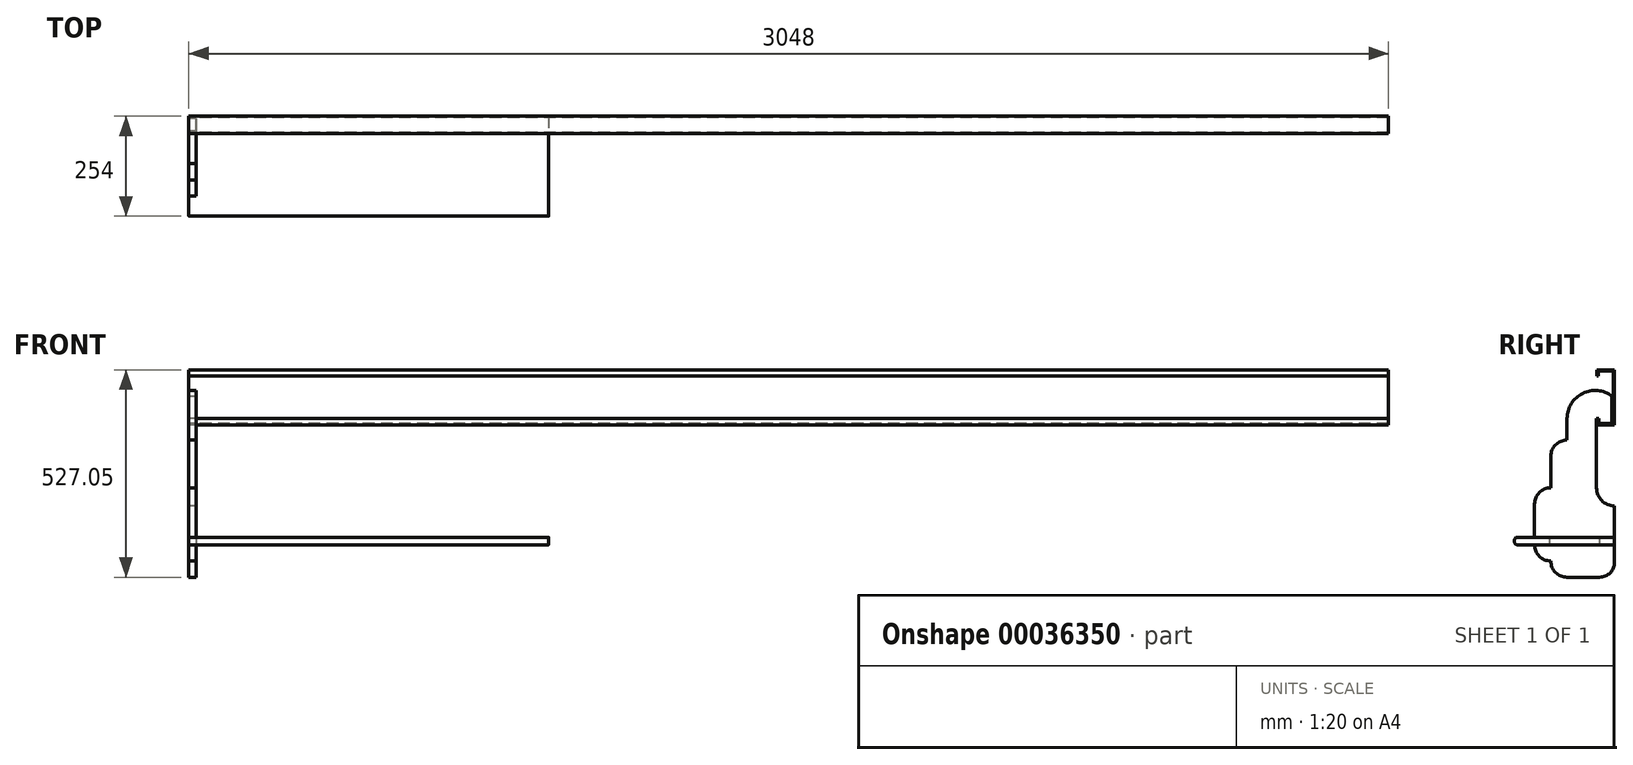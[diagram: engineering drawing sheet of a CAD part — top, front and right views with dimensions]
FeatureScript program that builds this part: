
annotation { "Feature Type Name" : "Feature", "Feature Type Description" : "" }
export const myFeature = defineFeature(function(context is Context, id is Id, definition is map)
    precondition{}
    {
        {
            var Q0;
            Q0=qCreatedBy(makeId("Right.planeOp"),FACE);
            var sketch = newSketch(context, id + "F0", { "sketchPlane" : qUnion([Q0])});
            skLineSegment(sketch, "E0", {"start": v(-44.45, 123.83) * mm, "end": v(-44.45, 139.7) * mm});
            skLineSegment(sketch, "E1", {"start": v(-44.45, 139.7) * mm, "end": v(0, 139.7) * mm});
            skLineSegment(sketch, "E2", {"start": v(0, 139.7) * mm, "end": v(0, 0) * mm});
            skLineSegment(sketch, "E3", {"start": v(0, 0) * mm, "end": v(-44.45, 0) * mm});
            skLineSegment(sketch, "E4", {"start": v(-44.45, 0) * mm, "end": v(-44.45, 15.88) * mm});
            skLineSegment(sketch, "E5", {"start": v(-44.45, 15.88) * mm, "end": v(-41.28, 15.88) * mm});
            skLineSegment(sketch, "E6", {"start": v(-41.28, 15.88) * mm, "end": v(-41.28, 3.18) * mm});
            skLineSegment(sketch, "E7", {"start": v(-41.28, 3.18) * mm, "end": v(-3.17, 3.18) * mm});
            skLineSegment(sketch, "E8", {"start": v(-3.17, 3.18) * mm, "end": v(-3.18, 136.53) * mm});
            skLineSegment(sketch, "E9", {"start": v(-3.18, 136.53) * mm, "end": v(-41.28, 136.53) * mm});
            skLineSegment(sketch, "E10", {"start": v(-41.28, 136.53) * mm, "end": v(-41.28, 123.83) * mm});
            skLineSegment(sketch, "E11", {"start": v(-41.28, 123.83) * mm, "end": v(-44.45, 123.83) * mm});
            skSolve(sketch);
        }
        {
            var Q0;
            Q0=makeQuery(id+"F0.imprint","IMPRINT",FACE,{"disambiguationData":[TD([[makeQuery(id+"F0.imprint","IMPRINT",EDGE,{"derivedFrom":sQuery(id+"F0.wireOp",EDGE,"E0")}),-1.0]])]});
            extrude(context, id + "F1", {"entities" : qUnion([Q0]), "depth" : 3048 * mm});
        }
        {
            var Q0;
            Q0=qCreatedBy(makeId("Right.planeOp"),FACE);
            var sketch = newSketch(context, id + "F2", { "sketchPlane" : qUnion([Q0])});
            skLineSegment(sketch, "E12.0", {"start": v(0, 139.7) * mm, "end": v(0, 0) * mm, "construction": true});
            skLineSegment(sketch, "E13", {"start": v(0, 0) * mm, "end": v(0, -410.1) * mm, "construction": true});
            skLineSegment(sketch, "E14.0", {"start": v(-3.17, 3.18) * mm, "end": v(-3.18, 136.53) * mm, "construction": true});
            skLineSegment(sketch, "E15", {"start": v(-3.17, 69.85) * mm, "end": v(-449.67, 69.85) * mm, "construction": true});
            skPoint(sketch, "E15.endSnap0", {"position": v(-3.17, 69.85) * mm});
            skLineSegment(sketch, "E16.bottom", {"start": v(0, -285.75) * mm, "end": v(-254, -285.75) * mm});
            skLineSegment(sketch, "E16.top", {"start": v(0, -304.8) * mm, "end": v(-254, -304.8) * mm});
            skLineSegment(sketch, "E16.left", {"start": v(0, -285.75) * mm, "end": v(0, -304.8) * mm});
            skLineSegment(sketch, "E16.right", {"start": v(-254, -285.75) * mm, "end": v(-254, -304.8) * mm});
            skSolve(sketch);
        }
        {
            var Q0;
            Q0=makeQuery(id+"F2.imprint","IMPRINT",FACE,{"disambiguationData":[TD([[makeQuery(id+"F2.imprint","IMPRINT",EDGE,{"derivedFrom":sQuery(id+"F2.wireOp",EDGE,"E16.bottom")}),1.0]])]});
            extrude(context, id + "F3", {"entities" : qUnion([Q0]), "depth" : 914.4 * mm});
        }
        {
            var Q0;
            Q0=qCreatedBy(makeId("Right.planeOp"),FACE);
            var sketch = newSketch(context, id + "F4", { "sketchPlane" : qUnion([Q0])});
            skLineSegment(sketch, "E17.0", {"start": v(-120.65, -304.8) * mm, "end": v(-165.1, -304.8) * mm, "construction": true});
            skLineSegment(sketch, "E18.0", {"start": v(-165.1, -285.75) * mm, "end": v(-254, -285.75) * mm, "construction": true});
            skLineSegment(sketch, "E19.0", {"start": v(0, 0) * mm, "end": v(-44.45, 0) * mm, "construction": true});
            skLineSegment(sketch, "E20.0", {"start": v(-44.45, 0) * mm, "end": v(-44.45, 15.88) * mm, "construction": true});
            skLineSegment(sketch, "E21.0", {"start": v(-44.45, 15.88) * mm, "end": v(-41.28, 15.88) * mm, "construction": true});
            skLineSegment(sketch, "E22.0", {"start": v(-41.28, 15.88) * mm, "end": v(-41.28, 3.18) * mm, "construction": true});
            skLineSegment(sketch, "E23.0", {"start": v(-41.28, 3.18) * mm, "end": v(-3.17, 3.18) * mm, "construction": true});
            skLineSegment(sketch, "E24.0", {"start": v(-3.17, 3.18) * mm, "end": v(-3.18, 136.53) * mm, "construction": true});
            skLineSegment(sketch, "E25", {"start": v(-165.1, -285.75) * mm, "end": v(-165.1, -135.91) * mm, "construction": true});
            skLineSegment(sketch, "E26", {"start": v(-120.65, 151.42) * mm, "end": v(-120.65, -259.76) * mm, "construction": true});
            skLineSegment(sketch, "E27", {"start": v(-203.2, -380.61) * mm, "end": v(-203.2, -295.28) * mm, "construction": true});
            skPoint(sketch, "E27.startSnap0", {"position": v(-203.2, -304.8) * mm});
            skLineSegment(sketch, "E28", {"start": v(0, 0) * mm, "end": v(0, -501.37) * mm, "construction": true});
            skLineSegment(sketch, "E29", {"start": v(-3.17, 15.88) * mm, "end": v(-120.65, 15.88) * mm, "construction": true});
            skArc(sketch, "E30", {"start": v(-6.35, 72.44) * mm, "mid": v(-81.14, 79.81) * mm, "end": v(-120.65, 15.88) * mm});
            skLineSegment(sketch, "E31", {"start": v(-120.65, 15.88) * mm, "end": v(-120.65, -38.94) * mm});
            skLineSegment(sketch, "E32", {"start": v(-120.65, -176.3) * mm, "end": v(-203.2, -176.3) * mm, "construction": true});
            skLineSegment(sketch, "E33", {"start": v(-161.92, -176.3) * mm, "end": v(-161.92, 52.78) * mm, "construction": true});
            skArc(sketch, "E34", {"start": v(-120.65, -38.94) * mm, "mid": v(-149.84, -51.03) * mm, "end": v(-161.92, -80.22) * mm});
            skLineSegment(sketch, "E35", {"start": v(-161.92, -80.22) * mm, "end": v(-161.92, -160.3) * mm});
            skArc(sketch, "E36", {"start": v(-161.92, -160.3) * mm, "mid": v(-191.11, -172.39) * mm, "end": v(-203.2, -201.57) * mm});
            skLineSegment(sketch, "E37", {"start": v(-203.2, -201.57) * mm, "end": v(-203.2, -285.75) * mm});
            skLineSegment(sketch, "E38.trimOffspring", {"start": v(-203.2, -285.75) * mm, "end": v(-203.2, -127.96) * mm, "construction": true});
            skLineSegment(sketch, "E39", {"start": v(-161.93, -176.3) * mm, "end": v(-161.92, -428.46) * mm, "construction": true});
            skLineSegment(sketch, "E40", {"start": v(-120.65, -259.76) * mm, "end": v(-120.65, -459.1) * mm, "construction": true});
            skLineSegment(sketch, "E41.trimOffspring", {"start": v(-203.2, -304.8) * mm, "end": v(-254, -304.8) * mm, "construction": true});
            skLineSegment(sketch, "E42", {"start": v(-120.65, -304.8) * mm, "end": v(-161.92, -304.8) * mm, "construction": true});
            skLineSegment(sketch, "E43", {"start": v(-161.92, -304.8) * mm, "end": v(-203.2, -304.8) * mm, "construction": true});
            skLineSegment(sketch, "E44", {"start": v(-161.92, -346.07) * mm, "end": v(0, -346.07) * mm, "construction": true});
            skArc(sketch, "E45", {"start": v(-161.92, -346.07) * mm, "mid": v(-149.84, -375.26) * mm, "end": v(-120.65, -387.35) * mm});
            skLineSegment(sketch, "E46", {"start": v(-120.65, -387.35) * mm, "end": v(-38.1, -387.35) * mm});
            skLineSegment(sketch, "E47", {"start": v(0, -349.25) * mm, "end": v(0, -304.8) * mm});
            skPoint(sketch, "E48.visualSharp", {"position": v(0, -387.35) * mm});
            skArc(sketch, "E48.filletArc", {"start": v(-38.1, -387.35) * mm, "mid": v(-11.16, -376.2) * mm, "end": v(0, -349.25) * mm});
            skArc(sketch, "E49.trimOffspring", {"start": v(-203.2, -304.8) * mm, "mid": v(-191.11, -333.99) * mm, "end": v(-161.92, -346.07) * mm});
            skLineSegment(sketch, "E50", {"start": v(-45.82, 15.88) * mm, "end": v(-45.82, -75.96) * mm});
            skLineSegment(sketch, "E51", {"start": v(-161.92, -160.3) * mm, "end": v(0, -160.3) * mm, "construction": true});
            skArc(sketch, "E52", {"start": v(-45.82, -160.3) * mm, "mid": v(-32.4, -192.7) * mm, "end": v(0, -206.11) * mm});
            skLineSegment(sketch, "E53", {"start": v(-45.82, -75.96) * mm, "end": v(-45.82, -160.3) * mm});
            skPoint(sketch, "E54.orphan", {"position": v(0, -209.55) * mm});
            skLineSegment(sketch, "E55", {"start": v(-203.2, -285.75) * mm, "end": v(-165.1, -285.75) * mm});
            skLineSegment(sketch, "E56", {"start": v(-165.1, -304.8) * mm, "end": v(-203.2, -304.8) * mm});
            skLineSegment(sketch, "E57", {"start": v(-45.82, 15.88) * mm, "end": v(-39.69, 15.88) * mm});
            skLineSegment(sketch, "E58", {"start": v(-39.69, 15.88) * mm, "end": v(-39.69, 3.18) * mm});
            skLineSegment(sketch, "E59", {"start": v(-39.69, 3.18) * mm, "end": v(-6.35, 3.18) * mm});
            skLineSegment(sketch, "E60", {"start": v(-6.35, 3.18) * mm, "end": v(-6.35, 72.44) * mm});
            skPoint(sketch, "E61.orphan", {"position": v(-3.18, 69.85) * mm});
            skLineSegment(sketch, "E62", {"start": v(0, -266.41) * mm, "end": v(-203.2, -266.41) * mm, "construction": true});
            skLineSegment(sketch, "E63", {"start": v(-165.1, -285.75) * mm, "end": v(-165.1, -304.8) * mm});
            skLineSegment(sketch, "E64.0", {"start": v(0, -285.75) * mm, "end": v(-254, -285.75) * mm, "construction": true});
            skLineSegment(sketch, "E65.0", {"start": v(0, -304.8) * mm, "end": v(-254, -304.8) * mm, "construction": true});
            skLineSegment(sketch, "E66", {"start": v(0, -285.75) * mm, "end": v(-38.1, -285.75) * mm});
            skLineSegment(sketch, "E67", {"start": v(-38.1, -285.75) * mm, "end": v(-38.1, -304.8) * mm});
            skLineSegment(sketch, "E68", {"start": v(-38.1, -304.8) * mm, "end": v(0, -304.8) * mm});
            skLineSegment(sketch, "E69.trimOffspring", {"start": v(0, -285.75) * mm, "end": v(0, -206.11) * mm});
            skLineSegment(sketch, "E70", {"start": v(-382.97, 87.18) * mm, "end": v(99.58, 87.18) * mm, "construction": true});
            skSolve(sketch);
        }
        {
            var Q0;
            Q0=makeQuery(id+"F4.imprint","IMPRINT",FACE,{"disambiguationData":[TD([[makeQuery(id+"F4.imprint","IMPRINT",EDGE,{"derivedFrom":sQuery(id+"F4.wireOp",EDGE,"E30")}),1.0]])]});
            extrude(context, id + "F5", {"entities" : qUnion([Q0]), "depth" : 19.05 * mm});
        }
        {
            var Q0;
            Q0=makeQuery(id+"F5.opExtrude","SWEPT_BODY",BODY,{"disambiguationData":[OSD([sQuery(id+"F4.wireOp",EDGE,"E30"),sQuery(id+"F4.wireOp",EDGE,"E31"),sQuery(id+"F4.wireOp",EDGE,"E34"),sQuery(id+"F4.wireOp",EDGE,"E35"),sQuery(id+"F4.wireOp",EDGE,"E36"),sQuery(id+"F4.wireOp",EDGE,"E37"),sQuery(id+"F4.wireOp",EDGE,"E45"),sQuery(id+"F4.wireOp",EDGE,"E46"),sQuery(id+"F4.wireOp",EDGE,"E47"),sQuery(id+"F4.wireOp",EDGE,"E48.filletArc"),sQuery(id+"F4.wireOp",EDGE,"E49.trimOffspring"),sQuery(id+"F4.wireOp",EDGE,"E50"),sQuery(id+"F4.wireOp",EDGE,"E52"),sQuery(id+"F4.wireOp",EDGE,"E53"),sQuery(id+"F4.wireOp",EDGE,"E55"),sQuery(id+"F4.wireOp",EDGE,"E56"),sQuery(id+"F4.wireOp",EDGE,"E57"),sQuery(id+"F4.wireOp",EDGE,"E58"),sQuery(id+"F4.wireOp",EDGE,"E59"),sQuery(id+"F4.wireOp",EDGE,"E60"),sQuery(id+"F4.wireOp",EDGE,"E63"),sQuery(id+"F4.wireOp",EDGE,"E66"),sQuery(id+"F4.wireOp",EDGE,"E67"),sQuery(id+"F4.wireOp",EDGE,"E68"),sQuery(id+"F4.wireOp",EDGE,"E69.trimOffspring")])]});
            var Q1;
            Q1=makeQuery(id+"F3.opExtrude","SWEPT_BODY",BODY,{"disambiguationData":[OSD([sQuery(id+"F2.wireOp",EDGE,"E16.bottom"),sQuery(id+"F2.wireOp",EDGE,"E16.top"),sQuery(id+"F2.wireOp",EDGE,"E16.left"),sQuery(id+"F2.wireOp",EDGE,"E16.right")])]});
            booleanBodies(context, id + "F6", {"operationType" : BooleanOperationType.SUBTRACTION, "tools" : qUnion([Q0]), "targets" : qUnion([Q1]), "keepTools" : true});
        }
        {
            var Q0;
            Q0=makeQuery(id+"F3.opExtrude","SWEPT_EDGE",EDGE,{"disambiguationData":[OSD([sQuery(id+"F2.wireOp",EDGE,"E16.bottom"),sQuery(id+"F2.wireOp",EDGE,"E16.right")])]});
            var Q1;
            Q1=makeQuery(id+"F3.opExtrude","SWEPT_EDGE",EDGE,{"disambiguationData":[OSD([sQuery(id+"F2.wireOp",EDGE,"E16.top"),sQuery(id+"F2.wireOp",EDGE,"E16.right")])]});
            fillet(context, id + "F7", {"entities" : qUnion([Q0, Q1]), "radius" : 6.35 * mm, "tangentPropagation" : true, "allowEdgeOverflow" : false});
        }
    });
